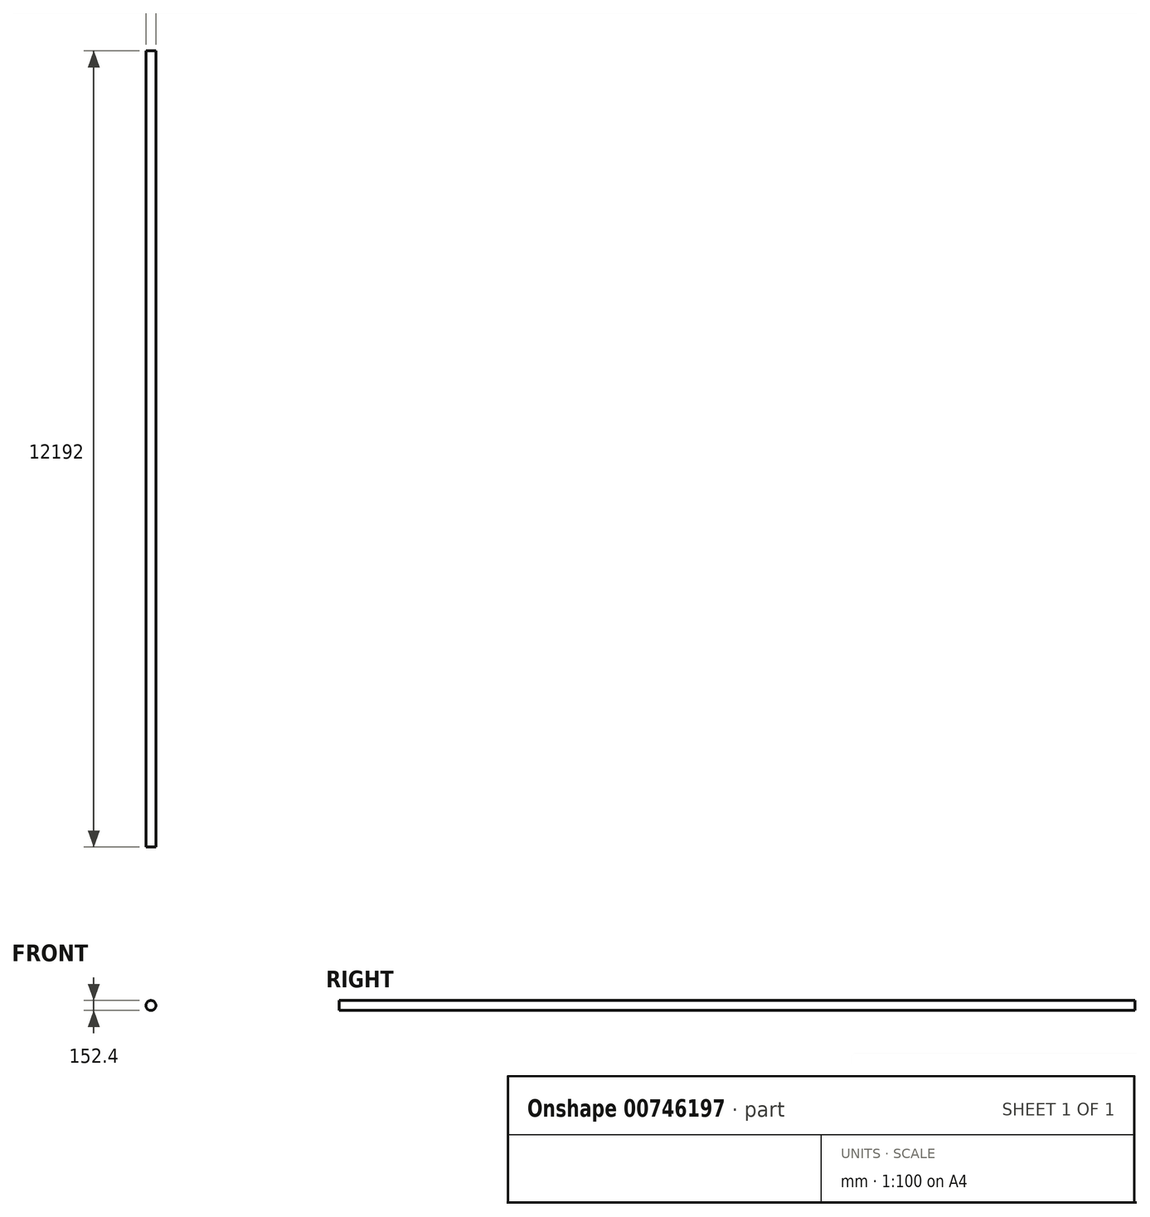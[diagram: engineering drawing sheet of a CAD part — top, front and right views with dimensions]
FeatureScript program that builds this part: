
annotation { "Feature Type Name" : "Feature", "Feature Type Description" : "" }
export const myFeature = defineFeature(function(context is Context, id is Id, definition is map)
    precondition{}
    {
        {
            var Q0;
            Q0=qCreatedBy(makeId("Front.planeOp"),FACE);
            var sketch = newSketch(context, id + "F0", { "sketchPlane" : qUnion([Q0])});
            skCircle(sketch, "E0", {"center": v(0, 0) * mm, "radius": 76.2 * mm});
            skSolve(sketch);
        }
        {
            var Q0;
            Q0=makeQuery(id+"F0.imprint","IMPRINT",FACE,{"disambiguationData":[TD([[makeQuery(id+"F0.imprint","IMPRINT",EDGE,{"derivedFrom":sQuery(id+"F0.wireOp",EDGE,"E0")}),1.0]])]});
            var Q1;
            Q1=sQuery(id+"F0.wireOp",EDGE,"E0");
            extrude(context, id + "F1", {"entities" : qUnion([Q0]), "surfaceEntities" : qUnion([Q1]), "depth" : 12192 * mm, "offsetDistance" : 30.48 * mm});
        }
    });
